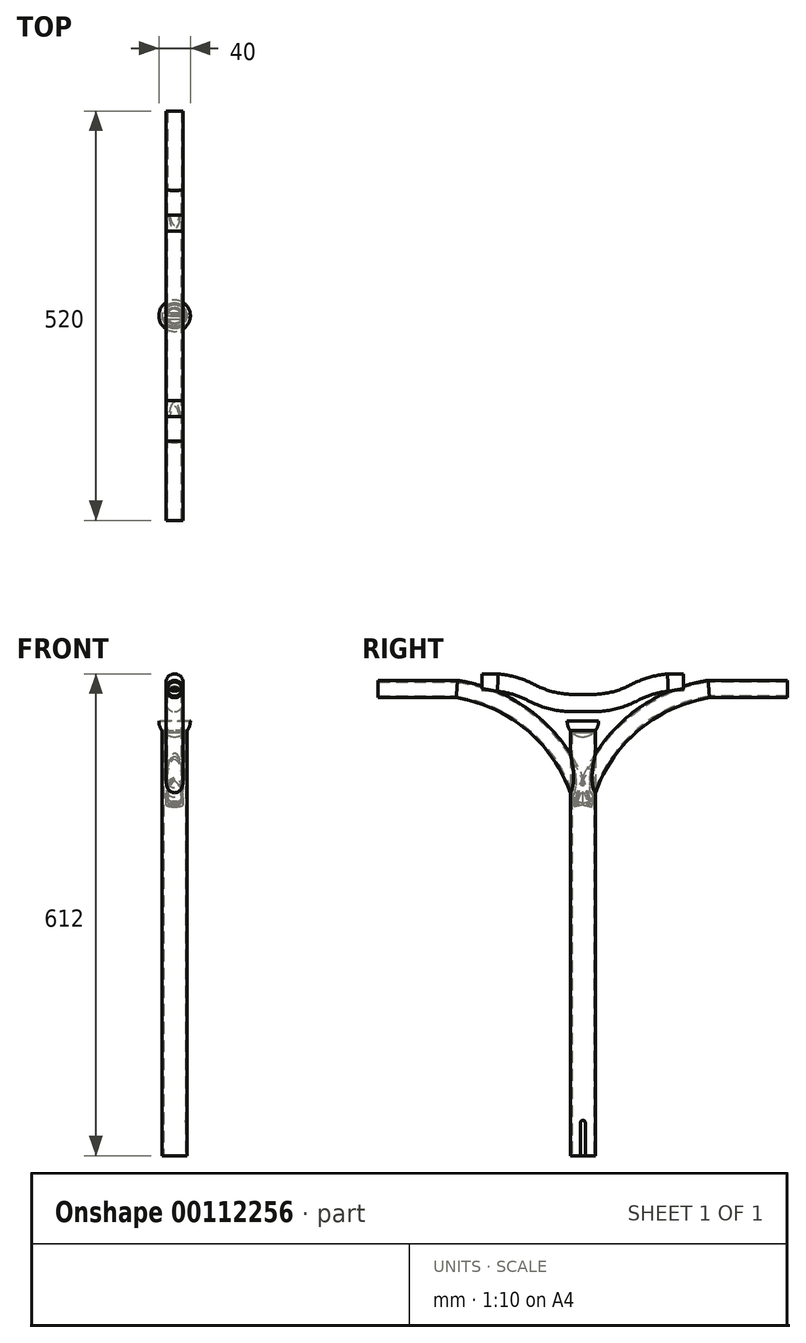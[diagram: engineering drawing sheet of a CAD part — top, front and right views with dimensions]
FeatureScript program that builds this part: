
annotation { "Feature Type Name" : "Feature", "Feature Type Description" : "" }
export const myFeature = defineFeature(function(context is Context, id is Id, definition is map)
    precondition{}
    {
        {
            var Q0;
            Q0=qCreatedBy(makeId("Top.planeOp"),FACE);
            var sketch = newSketch(context, id + "F0", { "sketchPlane" : qUnion([Q0])});
            skCircle(sketch, "E0", {"center": v(0, 0) * mm, "radius": 16 * mm});
            skSolve(sketch);
        }
        {
            var Q0;
            Q0 = qSketchRegion(id + "F0", true);
            extrude(context, id + "F1", {"entities" : qUnion([Q0]), "depth" : 550 * mm});
        }
        {
            var Q0;
            Q0=makeQuery(id+"F1.opExtrude","CAP_FACE",FACE,{"disambiguationData":[OSD([sQuery(id+"F0.wireOp",EDGE,"E0")])],"isStart":true});
            shell(context, id + "F2", {"entities" : qUnion([Q0]), "thickness" : 2 * mm});
        }
        {
            var Q0;
            Q0=qCreatedBy(makeId("Right.planeOp"),FACE);
            var sketch = newSketch(context, id + "F3", { "sketchPlane" : qUnion([Q0])});
            skLineSegment(sketch, "E1.bottom", {"start": v(-3, 0) * mm, "end": v(3, 0) * mm});
            skLineSegment(sketch, "E1.top", {"start": v(0, 45) * mm, "end": v(0, 45) * mm});
            skLineSegment(sketch, "E1.left", {"start": v(-3, 0) * mm, "end": v(-3, 42) * mm});
            skLineSegment(sketch, "E1.right", {"start": v(3, 0) * mm, "end": v(3, 42) * mm});
            skPoint(sketch, "E2.visualSharp", {"position": v(-3, 45) * mm});
            skArc(sketch, "E2.filletArc", {"start": v(0, 45) * mm, "mid": v(-2.12, 44.12) * mm, "end": v(-3, 42) * mm});
            skPoint(sketch, "E3.visualSharp", {"position": v(3, 45) * mm});
            skArc(sketch, "E3.filletArc", {"start": v(3, 42) * mm, "mid": v(2.12, 44.12) * mm, "end": v(0, 45) * mm});
            skSolve(sketch);
        }
        {
            var Q0;
            Q0 = qSketchRegion(id + "F3", true);
            extrude(context, id + "F4", {"entities" : qUnion([Q0]), "operationType" : NewBodyOperationType.REMOVE, "endBound" : BoundingType.THROUGH_ALL, "depth" : 25 * mm});
        }
        {
            var Q0;
            Q0=qCreatedBy(makeId("Right.planeOp"),FACE);
            var sketch = newSketch(context, id + "F5", { "sketchPlane" : qUnion([Q0])});
            skArc(sketch, "E4", {"start": v(160, 592.75) * mm, "mid": v(57.62, 543.58) * mm, "end": v(0, 445.72) * mm});
            skLineSegment(sketch, "E5", {"start": v(160, 592.75) * mm, "end": v(260, 592.75) * mm});
            skSolve(sketch);
        }
        {
            var Q0;
            Q0=sQuery(id+"F5.wireOp",VERTEX,"E5.end");
            var Q1;
            Q1=qCreatedBy(makeId("Front.planeOp"),FACE);
            cPlane(context, id + "F6", {"entities" : qUnion([Q0, Q1]), "cplaneType" : CPlaneType.PLANE_POINT, "offset" : 25 * mm, "width" : 150 * mm, "height" : 150 * mm});
        }
        {
            var Q0;
            Q0=qCreatedBy(id+"F6.planeOp",FACE);
            var sketch = newSketch(context, id + "F7", { "sketchPlane" : qUnion([Q0])});
            skCircle(sketch, "E6", {"center": v(0, 592.75) * mm, "radius": 11 * mm});
            skSolve(sketch);
        }
        {
            var Q0;
            Q0 = qSketchRegion(id + "F7", true);
            var Q1;
            Q1 = qConstructionFilter(qBodyType(qCreatedBy(id + "F5" ,EDGE), BodyType.WIRE), ConstructionObject.NO);
            sweep(context, id + "F8", {"operationType" : NewBodyOperationType.ADD, "profiles" : qUnion([Q0]), "path" : qUnion([Q1])});
        }
        {
            var Q0;
            Q0=makeQuery(id+"F8.opSweep","CAP_FACE",FACE,{"disambiguationData":[OSD([sQuery(id+"F5.wireOp",VERTEX,"E5.end"),sQuery(id+"F7.wireOp",EDGE,"E6")])],"isStart":true});
            shell(context, id + "F9", {"entities" : qUnion([Q0]), "thickness" : 2 * mm});
        }
        {
            var Q0;
            Q0=makeQuery(id+"F1.opExtrude","SWEPT_BODY",BODY,{"disambiguationData":[OSD([sQuery(id+"F0.wireOp",EDGE,"E0")])]});
            var Q1;
            Q1=qCreatedBy(makeId("Front.planeOp"),FACE);
            mirror(context, id + "F10", {"operationType" : NewBodyOperationType.ADD, "entities" : qUnion([Q0]), "mirrorPlane" : qUnion([Q1])});
        }
        {
            var Q0;
            Q0=qCreatedBy(makeId("Right.planeOp"),FACE);
            var sketch = newSketch(context, id + "F11", { "sketchPlane" : qUnion([Q0])});
            skLineSegment(sketch, "E7", {"start": v(0, 0) * mm, "end": v(0, 575) * mm, "construction": true});
            skLineSegment(sketch, "E8", {"start": v(0, 575) * mm, "end": v(-12.5, 575) * mm});
            skArc(sketch, "E9", {"start": v(-12.5, 575) * mm, "mid": v(-39.62, 578.33) * mm, "end": v(-65.13, 588.13) * mm});
            skArc(sketch, "E10", {"start": v(-65.13, 588.13) * mm, "mid": v(-85.93, 596.7) * mm, "end": v(-108, 601) * mm});
            skLineSegment(sketch, "E11", {"start": v(-108, 601) * mm, "end": v(-128, 601) * mm});
            skLineSegment(sketch, "E12.MirrorCS", {"start": v(108, 601) * mm, "end": v(128, 601) * mm});
            skArc(sketch, "E13.MirrorCS", {"start": v(65.13, 588.13) * mm, "mid": v(85.93, 596.7) * mm, "end": v(108, 601) * mm});
            skArc(sketch, "E14.MirrorCS", {"start": v(12.5, 575) * mm, "mid": v(39.62, 578.33) * mm, "end": v(65.13, 588.13) * mm});
            skLineSegment(sketch, "E15.MirrorCS", {"start": v(0, 575) * mm, "end": v(12.5, 575) * mm});
            skSolve(sketch);
        }
        {
            var Q0;
            Q0=sQuery(id+"F11.wireOp",VERTEX,"E12.MirrorCS.end");
            var Q1;
            Q1=qCreatedBy(id+"F6.planeOp",FACE);
            cPlane(context, id + "F12", {"entities" : qUnion([Q0, Q1]), "cplaneType" : CPlaneType.PLANE_POINT, "offset" : 25 * mm, "width" : 150 * mm, "height" : 150 * mm});
        }
        {
            var Q0;
            Q0=qCreatedBy(id+"F12.planeOp",FACE);
            var sketch = newSketch(context, id + "F13", { "sketchPlane" : qUnion([Q0])});
            skCircle(sketch, "E16", {"center": v(0, 601) * mm, "radius": 11 * mm});
            skSolve(sketch);
        }
        {
            var Q0;
            Q0 = qSketchRegion(id + "F13", true);
            var Q1;
            Q1 = qConstructionFilter(qBodyType(qCreatedBy(id + "F11" ,EDGE), BodyType.WIRE), ConstructionObject.NO);
            sweep(context, id + "F14", {"operationType" : NewBodyOperationType.ADD, "profiles" : qUnion([Q0]), "path" : qUnion([Q1])});
        }
        {
            var Q0;
            Q0=qCreatedBy(makeId("Right.planeOp"),FACE);
            var sketch = newSketch(context, id + "F15", { "sketchPlane" : qUnion([Q0])});
            skArc(sketch, "E17", {"start": v(-20, 552) * mm, "mid": v(-14.14, 537.86) * mm, "end": v(0, 532) * mm});
            skLineSegment(sketch, "E18", {"start": v(0, 552) * mm, "end": v(0, 532) * mm});
            skLineSegment(sketch, "E19", {"start": v(-20, 552) * mm, "end": v(0, 552) * mm});
            skSolve(sketch);
        }
        {
            var Q0;
            Q0 = qSketchRegion(id + "F15", true);
            var Q1;
            Q1=makeQuery(id+"F1.opExtrude","CAP_EDGE",EDGE,{"disambiguationData":[OSD([sQuery(id+"F0.wireOp",EDGE,"E0")])],"isStart":false});
            revolve(context, id + "F16", {"operationType" : NewBodyOperationType.ADD, "entities" : qUnion([Q0]), "axis" : qUnion([Q1]), "revolveType" : RevolveType.FULL});
        }
    });
